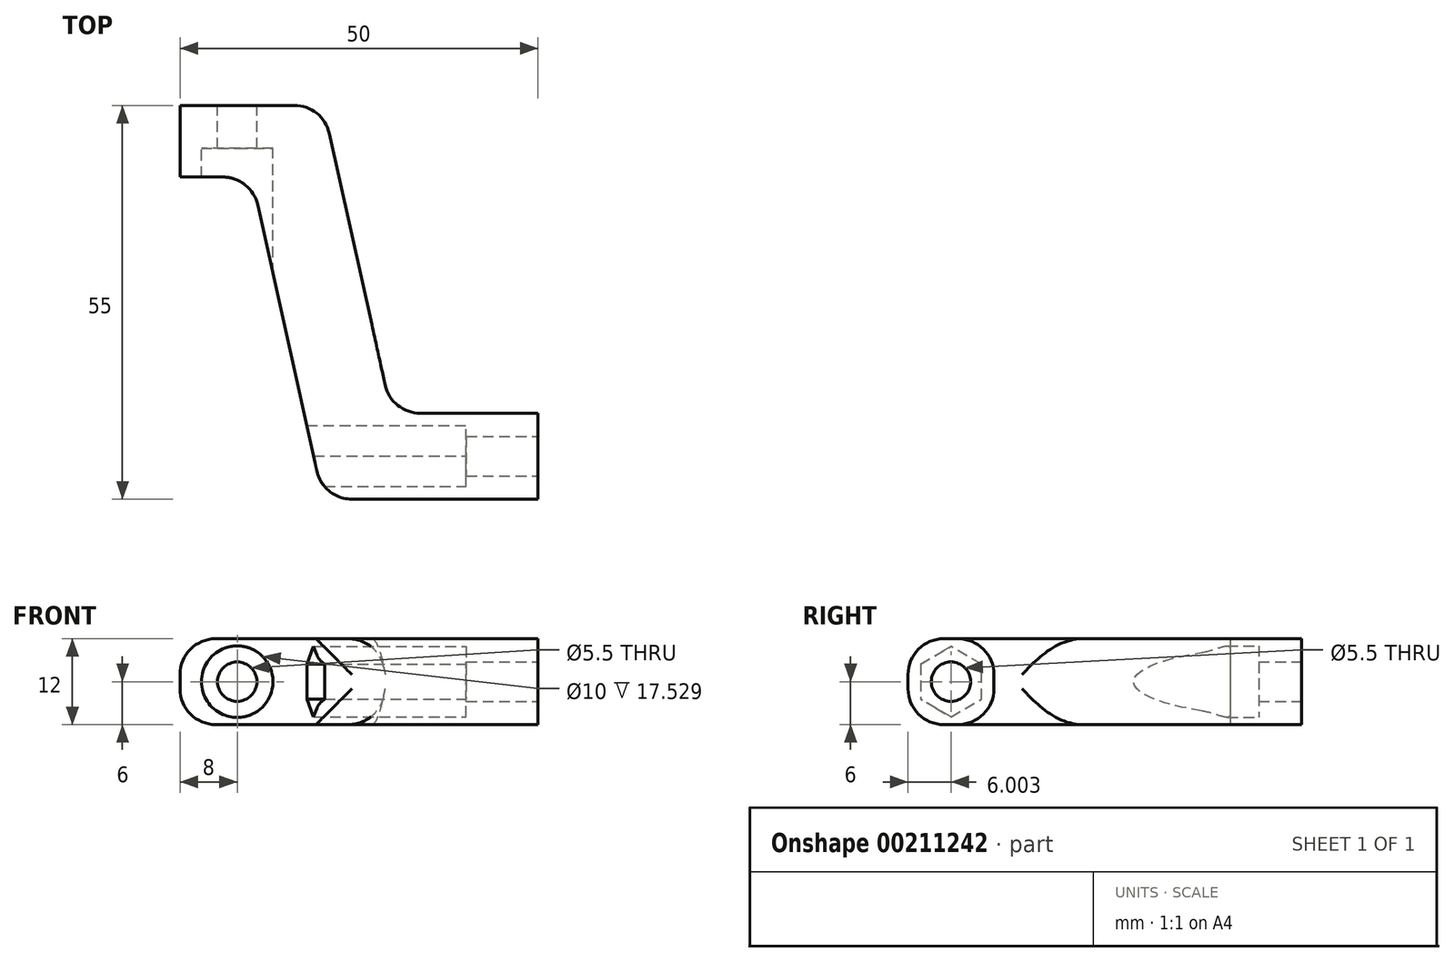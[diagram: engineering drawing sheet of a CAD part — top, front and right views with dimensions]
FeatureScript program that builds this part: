
annotation { "Feature Type Name" : "Feature", "Feature Type Description" : "" }
export const myFeature = defineFeature(function(context is Context, id is Id, definition is map)
    precondition{}
    {
        {
            var Q0;
            Q0=qCreatedBy(makeId("Top.planeOp"),FACE);
            var sketch = newSketch(context, id + "F0", { "sketchPlane" : qUnion([Q0])});
            skLineSegment(sketch, "E0", {"start": v(-25.27, 25.11) * mm, "end": v(-5.27, 25.11) * mm});
            skLineSegment(sketch, "E1", {"start": v(-5.27, 25.11) * mm, "end": v(4.29, -17.89) * mm});
            skLineSegment(sketch, "E2", {"start": v(4.29, -17.89) * mm, "end": v(24.73, -17.89) * mm});
            skLineSegment(sketch, "E3", {"start": v(24.73, -17.89) * mm, "end": v(24.73, -29.89) * mm});
            skLineSegment(sketch, "E4", {"start": v(24.73, -29.89) * mm, "end": v(-5.27, -29.89) * mm});
            skLineSegment(sketch, "E5", {"start": v(-5.27, -29.89) * mm, "end": v(-15.27, 15.11) * mm});
            skLineSegment(sketch, "E6", {"start": v(-15.27, 15.11) * mm, "end": v(-25.27, 15.11) * mm});
            skLineSegment(sketch, "E7", {"start": v(-25.27, 15.11) * mm, "end": v(-25.27, 25.11) * mm});
            skSolve(sketch);
        }
        {
            var Q0;
            Q0=makeQuery(id+"F0.imprint","IMPRINT",FACE,{"disambiguationData":[TD([[makeQuery(id+"F0.imprint","IMPRINT",EDGE,{"derivedFrom":sQuery(id+"F0.wireOp",EDGE,"E0")}),-1.0]])]});
            extrude(context, id + "F1", {"entities" : qUnion([Q0]), "depth" : 12 * mm});
        }
        {
            var Q0;
            Q0=makeQuery(id+"F1.opExtrude","SWEPT_FACE",FACE,{"disambiguationData":[OSD([sQuery(id+"F0.wireOp",EDGE,"E3")])]});
            var sketch = newSketch(context, id + "F2", { "sketchPlane" : qUnion([Q0])});
            skCircle(sketch, "E8", {"center": v(-23.89, 6) * mm, "radius": 2.75 * mm});
            skCircle(sketch, "E9.cCircle", {"center": v(-23.89, 6) * mm, "radius": 4.25 * mm, "construction": true});
            skLineSegment(sketch, "E9.0", {"start": v(-19.64, 8.45) * mm, "end": v(-19.64, 3.55) * mm});
            skLineSegment(sketch, "E9.1", {"start": v(-19.64, 3.55) * mm, "end": v(-23.89, 1.1) * mm});
            skLineSegment(sketch, "E9.2", {"start": v(-23.89, 1.1) * mm, "end": v(-28.14, 3.55) * mm});
            skLineSegment(sketch, "E9.3", {"start": v(-28.14, 3.55) * mm, "end": v(-28.14, 8.45) * mm});
            skLineSegment(sketch, "E9.4", {"start": v(-28.14, 8.45) * mm, "end": v(-23.89, 10.9) * mm});
            skLineSegment(sketch, "E9.5", {"start": v(-23.89, 10.9) * mm, "end": v(-19.64, 8.45) * mm});
            skPoint(sketch, "E9.0.midPoint", {"position": v(-19.64, 6) * mm});
            skSolve(sketch);
        }
        {
            var Q0;
            Q0=makeQuery(id+"F2.imprint","IMPRINT",FACE,{"disambiguationData":[TD([[makeQuery(id+"F2.imprint","IMPRINT",EDGE,{"derivedFrom":sQuery(id+"F2.wireOp",EDGE,"E8")}),-1.0]])]});
            extrude(context, id + "F3", {"entities" : qUnion([Q0]), "operationType" : NewBodyOperationType.REMOVE, "endBound" : BoundingType.THROUGH_ALL, "oppositeDirection" : true, "depth" : 25 * mm, "hasSecondDirection" : true, "secondDirectionOppositeDirection" : true, "secondDirectionDepth" : 10 * mm});
        }
        {
            var Q0;
            Q0=makeQuery(id+"F2.imprint","IMPRINT",FACE,{"disambiguationData":[TD([[makeQuery(id+"F2.imprint","IMPRINT",EDGE,{"derivedFrom":sQuery(id+"F2.wireOp",EDGE,"E8")}),1.0]])]});
            extrude(context, id + "F4", {"entities" : qUnion([Q0]), "operationType" : NewBodyOperationType.REMOVE, "endBound" : BoundingType.THROUGH_ALL, "oppositeDirection" : true, "depth" : 25 * mm});
        }
        {
            var Q0;
            Q0=makeQuery(id+"F1.opExtrude","SWEPT_FACE",FACE,{"disambiguationData":[OSD([sQuery(id+"F0.wireOp",EDGE,"E0")])]});
            var sketch = newSketch(context, id + "F5", { "sketchPlane" : qUnion([Q0])});
            skCircle(sketch, "E10", {"center": v(17.27, 6) * mm, "radius": 2.75 * mm});
            skPoint(sketch, "E10.centerSnap0", {"position": v(25.27, 6) * mm});
            skCircle(sketch, "E11", {"center": v(17.27, 6) * mm, "radius": 5 * mm});
            skSolve(sketch);
        }
        {
            var Q0;
            Q0=makeQuery(id+"F5.imprint","IMPRINT",FACE,{"disambiguationData":[TD([[makeQuery(id+"F5.imprint","IMPRINT",EDGE,{"derivedFrom":sQuery(id+"F5.wireOp",EDGE,"E10")}),1.0]])]});
            extrude(context, id + "F6", {"entities" : qUnion([Q0]), "operationType" : NewBodyOperationType.REMOVE, "endBound" : BoundingType.THROUGH_ALL, "oppositeDirection" : true, "depth" : 25 * mm});
        }
        {
            var Q0;
            Q0=makeQuery(id+"F5.imprint","IMPRINT",FACE,{"disambiguationData":[TD([[makeQuery(id+"F5.imprint","IMPRINT",EDGE,{"derivedFrom":sQuery(id+"F5.wireOp",EDGE,"E10")}),-1.0]])]});
            extrude(context, id + "F7", {"entities" : qUnion([Q0]), "operationType" : NewBodyOperationType.REMOVE, "endBound" : BoundingType.THROUGH_ALL, "oppositeDirection" : true, "depth" : 25 * mm, "hasSecondDirection" : true, "secondDirectionOppositeDirection" : true, "secondDirectionDepth" : 6 * mm});
        }
        {
            var Q0;
            Q0=makeQuery(id+"F1.opExtrude","CAP_EDGE",EDGE,{"disambiguationData":[OSD([sQuery(id+"F0.wireOp",EDGE,"E4")])],"isStart":false});
            var Q1;
            Q1=makeQuery(id+"F1.opExtrude","CAP_EDGE",EDGE,{"disambiguationData":[OSD([sQuery(id+"F0.wireOp",EDGE,"E4")])],"isStart":true});
            var Q2;
            Q2=makeQuery(id+"F1.opExtrude","CAP_EDGE",EDGE,{"disambiguationData":[OSD([sQuery(id+"F0.wireOp",EDGE,"E7")])],"isStart":false});
            var Q3;
            Q3=makeQuery(id+"F1.opExtrude","CAP_EDGE",EDGE,{"disambiguationData":[OSD([sQuery(id+"F0.wireOp",EDGE,"E7")])],"isStart":true});
            var Q4;
            Q4=makeQuery(id+"F1.opExtrude","CAP_EDGE",EDGE,{"disambiguationData":[OSD([sQuery(id+"F0.wireOp",EDGE,"E2")])],"isStart":false});
            var Q5;
            Q5=makeQuery(id+"F1.opExtrude","CAP_EDGE",EDGE,{"disambiguationData":[OSD([sQuery(id+"F0.wireOp",EDGE,"E2")])],"isStart":true});
            var Q6;
            Q6=makeQuery(id+"F1.opExtrude","SWEPT_EDGE",EDGE,{"disambiguationData":[OSD([sQuery(id+"F0.wireOp",EDGE,"E4"),sQuery(id+"F0.wireOp",EDGE,"E5")])]});
            var Q7;
            Q7=makeQuery(id+"F1.opExtrude","SWEPT_EDGE",EDGE,{"disambiguationData":[OSD([sQuery(id+"F0.wireOp",EDGE,"E1"),sQuery(id+"F0.wireOp",EDGE,"E2")])]});
            var Q8;
            Q8=makeQuery(id+"F1.opExtrude","SWEPT_EDGE",EDGE,{"disambiguationData":[OSD([sQuery(id+"F0.wireOp",EDGE,"E0"),sQuery(id+"F0.wireOp",EDGE,"E1")])]});
            var Q9;
            {var subQ0=sQuery(id+"F0.wireOp",EDGE,"E6");var subQ1=sQuery(id+"F0.wireOp",EDGE,"E5");Q9=makeQuery(id+"F6.boolean.opBoolean","SPLIT",EDGE,{"disambiguationData":[TD([makeQuery(id+"F1.opExtrude","CAP_FACE",FACE,{"disambiguationData":[OSD([sQuery(id+"F0.wireOp",EDGE,"E0"),sQuery(id+"F0.wireOp",EDGE,"E1"),sQuery(id+"F0.wireOp",EDGE,"E2"),sQuery(id+"F0.wireOp",EDGE,"E3"),sQuery(id+"F0.wireOp",EDGE,"E4"),subQ1,subQ0,sQuery(id+"F0.wireOp",EDGE,"E7")])],"isStart":true})])],"derivedFrom":makeQuery(id+"F1.opExtrude","SWEPT_EDGE",EDGE,{"disambiguationData":[OSD([subQ1,subQ0])]})});}
            var Q10;
            {var subQ0=sQuery(id+"F0.wireOp",EDGE,"E6");var subQ1=sQuery(id+"F0.wireOp",EDGE,"E5");Q10=makeQuery(id+"F6.boolean.opBoolean","SPLIT",EDGE,{"disambiguationData":[TD([makeQuery(id+"F1.opExtrude","CAP_FACE",FACE,{"disambiguationData":[OSD([sQuery(id+"F0.wireOp",EDGE,"E0"),sQuery(id+"F0.wireOp",EDGE,"E1"),sQuery(id+"F0.wireOp",EDGE,"E2"),sQuery(id+"F0.wireOp",EDGE,"E3"),sQuery(id+"F0.wireOp",EDGE,"E4"),subQ1,subQ0,sQuery(id+"F0.wireOp",EDGE,"E7")])],"isStart":false})])],"derivedFrom":makeQuery(id+"F1.opExtrude","SWEPT_EDGE",EDGE,{"disambiguationData":[OSD([subQ1,subQ0])]})});}
            fillet(context, id + "F8", {"entities" : qUnion([Q0, Q1, Q2, Q3, Q4, Q5, Q6, Q7, Q8, Q9, Q10]), "radius" : 5 * mm, "tangentPropagation" : true, "allowEdgeOverflow" : false});
        }
    });
